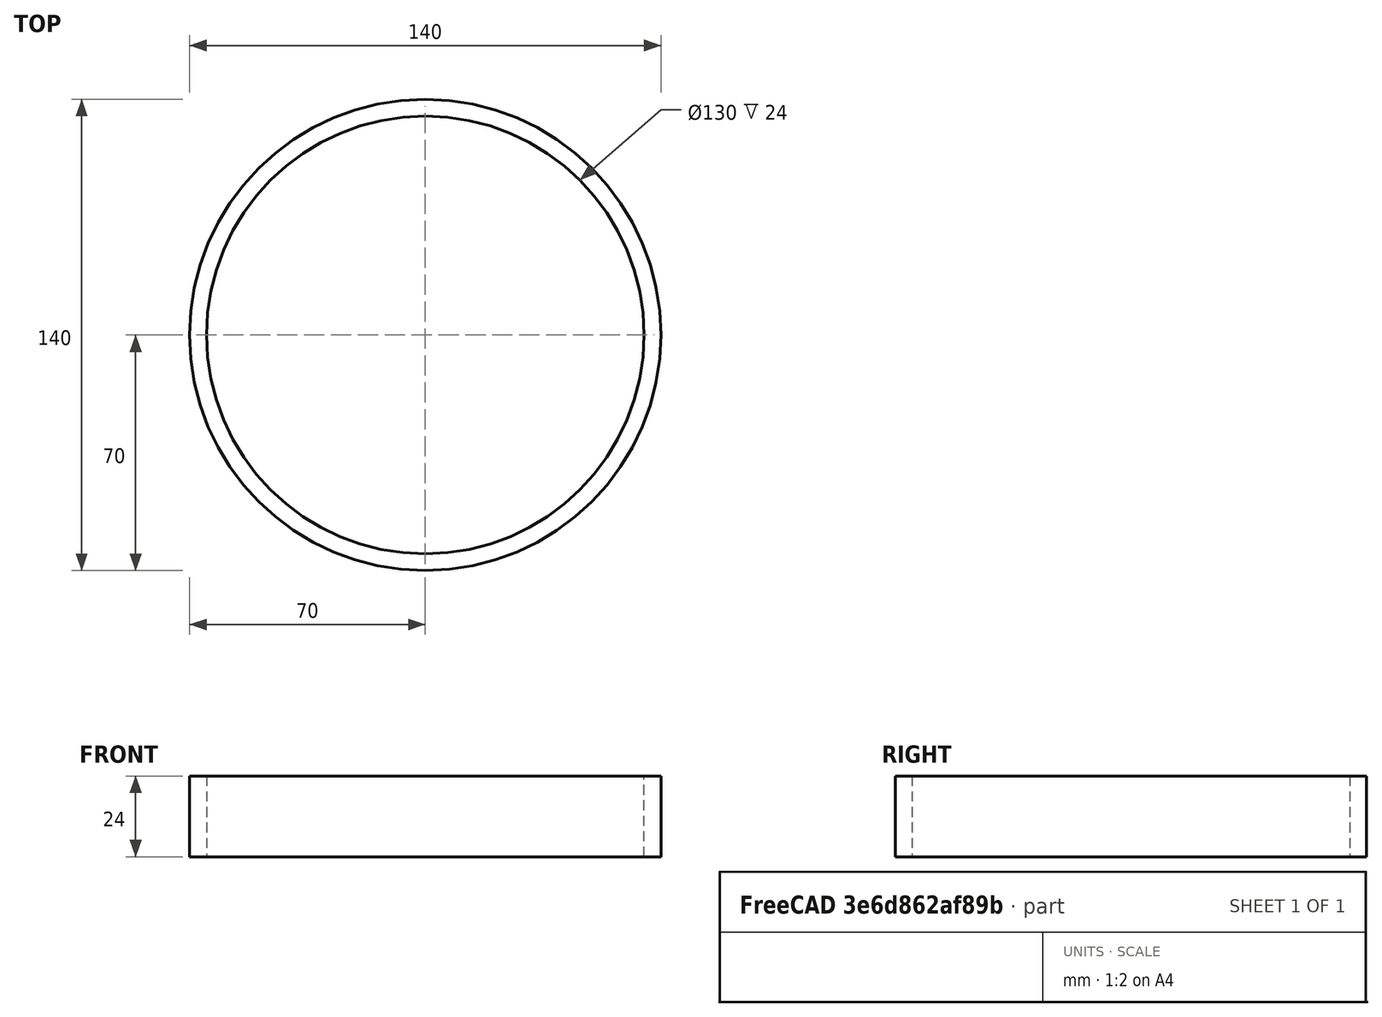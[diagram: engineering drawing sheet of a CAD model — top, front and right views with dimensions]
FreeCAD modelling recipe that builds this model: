
FCSTD DOCUMENT  (FreeCAD 0.19R24276 (Git))
Label: Ring_130x140x24_OUT
License: All rights reserved
LicenseURL: http://en.wikipedia.org/wiki/All_rights_reserved
objects: Sketcher::SketchObject×1, PartDesign::Pad×1, PartDesign::Body×1
note: 4 computed .brp shape members not serialized (recipe doc carries the construction recipe); baked Part::Feature solids carry a one-line shape summary decoded from their .brp

FEATURE [Sketcher::SketchObject] Sketch
  FullyConstrained = true
  MapMode = 5
  Support = -> [XY_Plane]
  sketch-geometry (2):
    g0: Circle CenterX=0 CenterY=0 CenterZ=0 NormalX=0 NormalY=0 NormalZ=1 AngleXU=0 Radius=65
    g1: Circle CenterX=0 CenterY=0 CenterZ=0 NormalX=0 NormalY=0 NormalZ=1 AngleXU=0 Radius=70
  constraints (4):
    c: Coincident(g1,g0)
    c: Diameter(g1) = 140
    c: Diameter(g0) = 130
    c: Coincident(g0,g-1)
FEATURE [PartDesign::Pad] Pad
  Direction = (1,1,1)
  Length = 24
  Length2 = 100
  Profile = -> Sketch
  Type = 0
FEATURE [PartDesign::Body] Body  label="Body_ring_out"
  Group = -> [Sketch,Pad]
  Origin = -> Origin
  Tip = -> Pad
